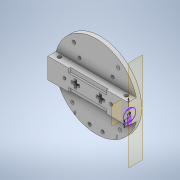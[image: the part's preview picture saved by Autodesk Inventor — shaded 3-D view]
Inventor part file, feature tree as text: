
AUTODESK INVENTOR PART (.ipt)
format: ipt  version: 2021 (Build 250183000, 183)  size: 360,448 bytes
history: native  units: mm
features: sketch x16, extrude x13, direct_edit x10, other x10, reference x9, move_body x8, plane x3, fillet x2, mirror x2
ambient origin geometry x8: Origin, YZ Plane, XZ Plane, XY Plane, X Axis, Y Axis, Z Axis, Center Point
bodies: Solid1 (feature_tree)
feature tree (73):
  sketch  "Sketch1"  dims[d0=100.0mm d1=5.0mm d2=0.0mm]
  extrude  "Extrusion1"  Depth=5.0mm TaperAngle=0.0deg
  extrude  "Extrusion2"  Depth=5.0mm
  extrude  "Extrusion3"  Depth=2.0mm
  fillet  "Fillet1"  Radius=2.0mm
  fillet  "Fillet2"  Radius=10.0mm
  extrude  "Extrusion4"  Depth=3.0mm
  extrude  "Extrusion5"  Depth=10.0mm TaperAngle=0.0deg
  plane  "Work Plane1"
  sketch  "Sketch8"  dims[d23=10.0mm d24=3.0mm]
  plane  "Work Plane3"
  extrude  "Extrusion7"  Depth=10.0mm
  plane  "Work Plane2"
  sketch  "Sketch10"  dims[d29=4.0mm d30=8.0mm]
  extrude  "Extrusion9"  Depth=3.0mm
  extrude  "Extrusion10"  Depth=3.0mm
  mirror  "Mirror3"
  extrude  "Extrusion11"  Depth=8.0mm
  extrude  "Extrusion12"  Depth=3.0mm
  extrude  "Extrusion13"  Depth=8.0mm
  direct_edit  "Direct Edit1"
  direct_edit  "Direct Edit2"
  direct_edit  "Direct Edit3"
  direct_edit  "Direct Edit4"
  direct_edit  "Direct Edit5"
  extrude  "Extrusion14"  Depth=51.75mm TaperAngle=0.0deg
  extrude  "Extrusion15"  Depth=7.0mm
  mirror  "Mirror4"
  direct_edit  "Direct Edit6"
  direct_edit  "Direct Edit7"
  direct_edit  "Direct Edit8"
  direct_edit  "Direct Edit9"
  direct_edit  "Direct Edit10"
  sketch  "Sketch2"  dims[d3=5.0mm d4=0.0mm d5=78.0mm]
  sketch  "Sketch3"  dims[d6=3.0mm d7=0.0mm d8=2.0mm d9=2.0mm d12=10.0mm d13=0.0mm]
  reference  "Reference1"
  reference  "Reference2"
  reference  "Reference3"
  reference  "Reference4"
  sketch  "Sketch4"  dims[d15=15.0mm d17=3.0mm]
  reference  "Reference5"
  sketch  "Sketch5"  dims[d18=10.0mm d19=10.0mm d20=0.0mm]
  sketch  "Sketch6"  dims[d21=3.0mm d22=10.0mm]
  sketch  "Sketch9"  dims[d25=10.0mm d26=3.0mm]
  sketch  "Sketch11"  dims[d33=3.0mm d34=0.0mm d35=4.0mm]
  reference  "Reference6"
  reference  "Reference7"
  reference  "Reference8"
  reference  "Reference9"
  sketch  "Sketch12"  dims[d38=10.0mm d39=0.0mm d40=8.0mm]
  sketch  "Sketch13"  dims[d41=3.2mm d42=51.75mm d43=0.0mm]
  sketch  "Sketch14"  dims[d44=30.75mm d45=0.0mm d46=7.0mm]
  sketch  "Sketch15"  dims[d47=1.0mm]
  sketch  "Sketch16"  dims[d48=9.0mm]
  sketch  "Sketch17"  dims[d49=1.0mm d50=9.0mm d51=30.75mm d52=0.0mm d53=10.0mm d54=0.0mm d55=0.0mm d56=0.0mm d57=-40.0mm d58=0.0mm d59=0.0mm d60=4.75mm d61=-32.5mm d62=0.0mm d63=0.0mm d64=2.0mm d65=-2.0mm d66=5.0mm d67=5.0mm d68=2.0mm d69=0.0mm d70=85.0mm d71=33.0mm d72=4.0mm d73=4.0mm d74=28.0mm d75=0.0mm d76=0.0mm d77=1.5mm d78=0.0mm d79=0.0mm d80=1.0mm d81=0.0mm d82=-0.5mm d83=-0.5mm d84=2.0mm d85=2.0mm d86=0.0mm d87=0.0mm d88=2.0mm d89=0.0mm d90=-2.0mm d91=0.0mm d92=0.0mm]
  parser-record x1  (decoder bookkeeping rows leaked as tree rows — omitted from the tree; the rows remain in map.json)
  other  "whole_assembly.iam"
  other  "539636 HGP-16-A-B-SSK---(asm_0_-ZH):1"
  other  "gripper extension:1"
  other  "Part3:1"
  move_body  "Move1"
  move_body  "Move2"
  move_body  "Move3"
  other  "Size1"
  other  "Delete1"
  other  "Size2"
  move_body  "Move4"
  move_body  "Move5"
  other  "Size3"
  other  "Size4"
  move_body  "Move6"
  move_body  "Move7"
  move_body  "Move8"
note: 1 file-system path scrubbed to <path> (originals preserved in map.json)
